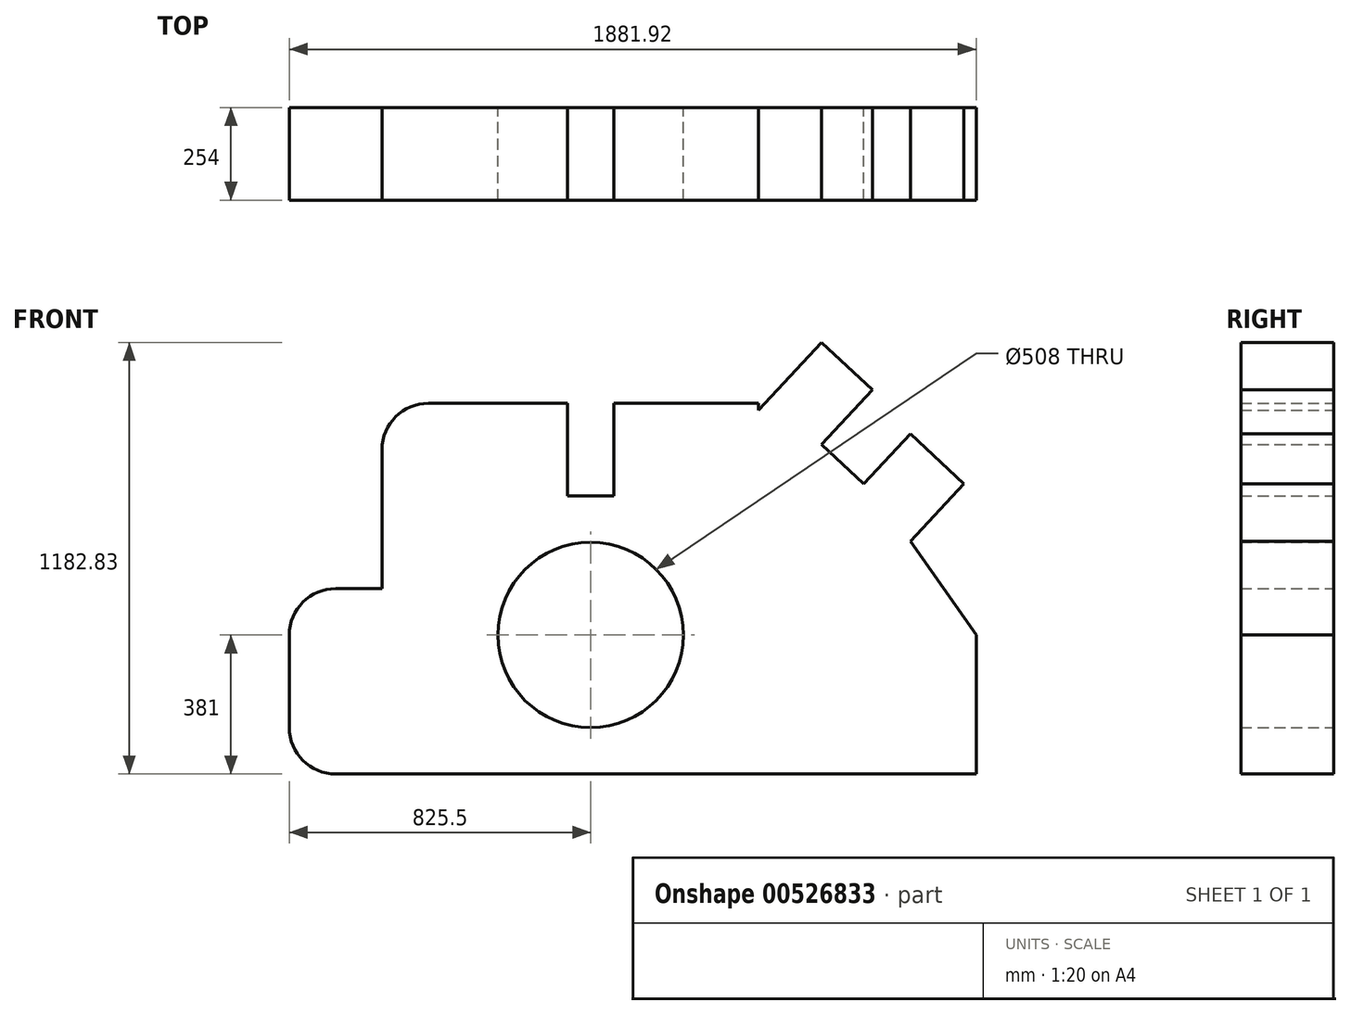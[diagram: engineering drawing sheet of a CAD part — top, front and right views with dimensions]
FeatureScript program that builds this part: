
annotation { "Feature Type Name" : "Feature", "Feature Type Description" : "" }
export const myFeature = defineFeature(function(context is Context, id is Id, definition is map)
    precondition{}
    {
        {
            var Q0;
            Q0=qCreatedBy(makeId("Front.planeOp"),FACE);
            var sketch = newSketch(context, id + "F0", { "sketchPlane" : qUnion([Q0])});
            skLineSegment(sketch, "E0", {"start": v(-100.33, 0) * mm, "end": v(1550.67, 0) * mm});
            skLineSegment(sketch, "E1", {"start": v(-227.33, 127) * mm, "end": v(-227.33, 381) * mm});
            skLineSegment(sketch, "E2", {"start": v(1654.6, 0) * mm, "end": v(1654.6, 381) * mm});
            skCircle(sketch, "E3", {"center": v(598.17, 381) * mm, "radius": 254 * mm});
            skLineSegment(sketch, "E4", {"start": v(-100.33, 508) * mm, "end": v(26.67, 508) * mm});
            skLineSegment(sketch, "E5", {"start": v(26.67, 508) * mm, "end": v(26.67, 889) * mm});
            skLineSegment(sketch, "E6", {"start": v(153.67, 1016) * mm, "end": v(534.67, 1016) * mm});
            skLineSegment(sketch, "E7", {"start": v(534.67, 1016) * mm, "end": v(534.67, 762) * mm});
            skLineSegment(sketch, "E8", {"start": v(534.67, 762) * mm, "end": v(661.67, 762) * mm});
            skLineSegment(sketch, "E9", {"start": v(661.67, 762) * mm, "end": v(661.67, 1016) * mm});
            skLineSegment(sketch, "E10", {"start": v(803.51, 1016) * mm, "end": v(1057.51, 1016) * mm});
            skLineSegment(sketch, "E11", {"start": v(1057.51, 997.27) * mm, "end": v(1230.95, 1182.83) * mm});
            skLineSegment(sketch, "E12", {"start": v(1230.95, 1182.83) * mm, "end": v(1370.42, 1052.48) * mm});
            skLineSegment(sketch, "E13", {"start": v(1370.42, 1052.48) * mm, "end": v(1230.95, 903.25) * mm});
            skLineSegment(sketch, "E14", {"start": v(1230.95, 903.25) * mm, "end": v(1346.84, 794.94) * mm});
            skLineSegment(sketch, "E15", {"start": v(1346.84, 794.94) * mm, "end": v(1474.77, 931.83) * mm});
            skLineSegment(sketch, "E16", {"start": v(1474.77, 931.83) * mm, "end": v(1621.23, 794.94) * mm});
            skLineSegment(sketch, "E17", {"start": v(1621.23, 794.94) * mm, "end": v(1474.77, 638.24) * mm});
            skLineSegment(sketch, "E18", {"start": v(1474.77, 638.24) * mm, "end": v(1654.6, 381) * mm});
            skLineSegment(sketch, "E19", {"start": v(1057.51, 1016) * mm, "end": v(1057.51, 997.27) * mm});
            skLineSegment(sketch, "E20", {"start": v(661.67, 1016) * mm, "end": v(803.51, 1016) * mm});
            skPoint(sketch, "E21.visualSharp", {"position": v(26.67, 1016) * mm});
            skArc(sketch, "E21.filletArc", {"start": v(33.02, 1016) * mm, "mid": v(28.53, 1014.14) * mm, "end": v(26.67, 1009.65) * mm});
            skArc(sketch, "E22.filletArc", {"start": v(153.67, 1016) * mm, "mid": v(63.87, 978.8) * mm, "end": v(26.67, 889) * mm});
            skPoint(sketch, "E23.visualSharp", {"position": v(-227.33, 508) * mm});
            skArc(sketch, "E23.filletArc", {"start": v(-100.33, 508) * mm, "mid": v(-190.13, 470.8) * mm, "end": v(-227.33, 381) * mm});
            skPoint(sketch, "E24.visualSharp", {"position": v(-227.33, 0) * mm});
            skArc(sketch, "E24.filletArc", {"start": v(-227.33, 127) * mm, "mid": v(-190.13, 37.2) * mm, "end": v(-100.33, 0) * mm});
            skLineSegment(sketch, "E25", {"start": v(1550.67, 0) * mm, "end": v(1654.6, 0) * mm});
            skSolve(sketch);
        }
        {
            var Q0;
            Q0 = qSketchRegion(id + "F0", true);
            extrude(context, id + "F1", {"entities" : qUnion([Q0]), "depth" : 254 * mm, "offsetDistance" : 25.4 * mm});
        }
    });
